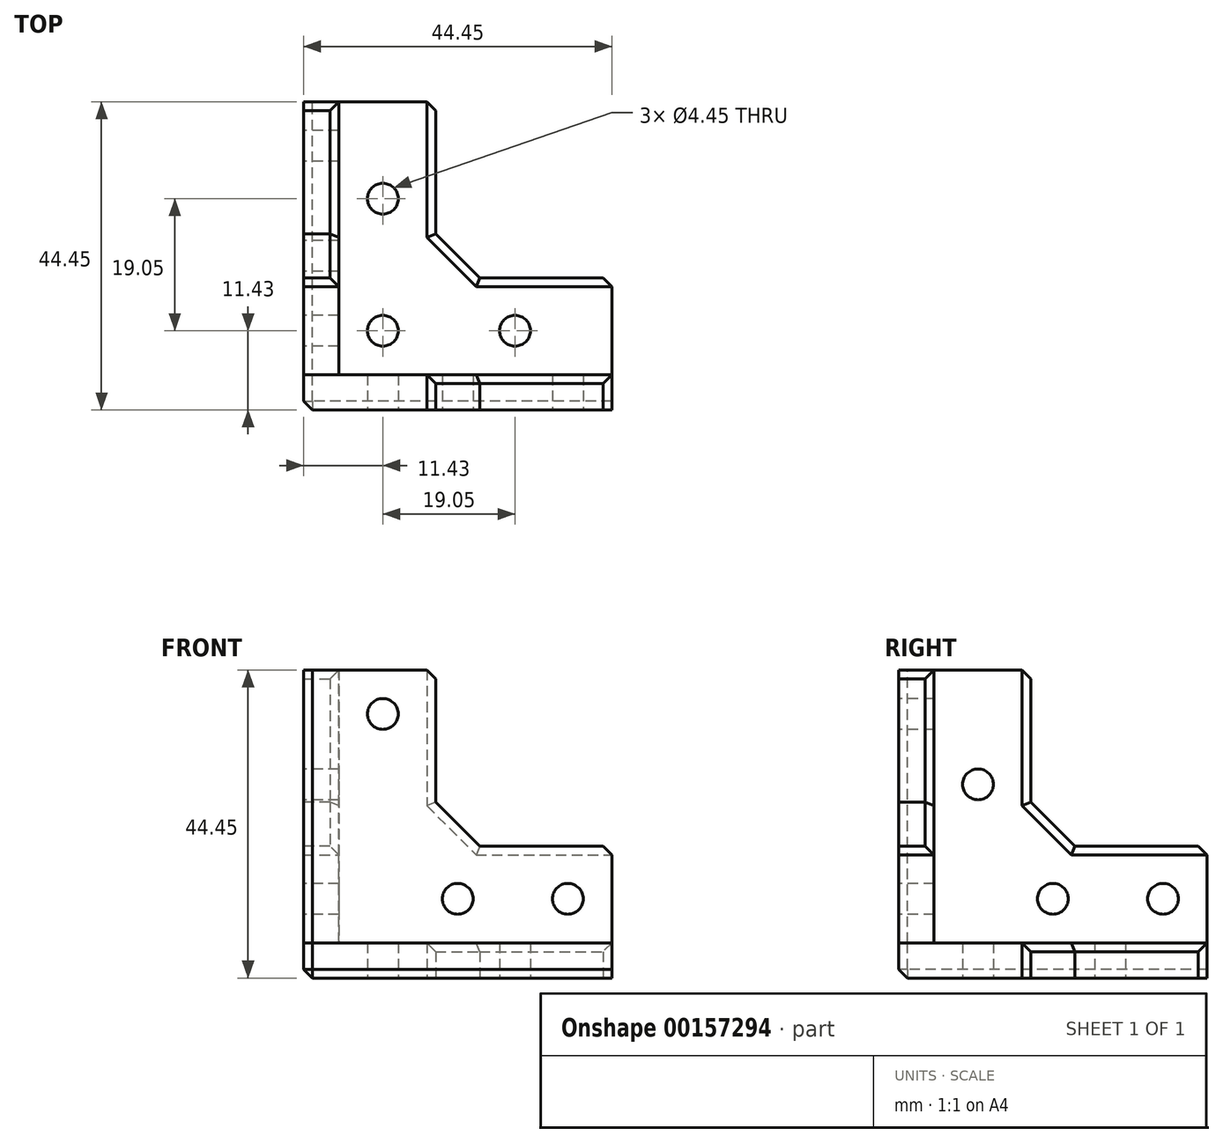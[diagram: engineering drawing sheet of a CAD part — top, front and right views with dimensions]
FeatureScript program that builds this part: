
annotation { "Feature Type Name" : "Feature", "Feature Type Description" : "" }
export const myFeature = defineFeature(function(context is Context, id is Id, definition is map)
    precondition{}
    {
        {
            var Q0;
            Q0=qCreatedBy(makeId("Top.planeOp"),FACE);
            var sketch = newSketch(context, id + "F0", { "sketchPlane" : qUnion([Q0])});
            skLineSegment(sketch, "E0", {"start": v(0, 0) * mm, "end": v(0, 44.45) * mm});
            skLineSegment(sketch, "E1", {"start": v(0, 44.45) * mm, "end": v(19.05, 44.45) * mm});
            skLineSegment(sketch, "E2", {"start": v(19.05, 44.45) * mm, "end": v(19.05, 25.4) * mm});
            skLineSegment(sketch, "E3", {"start": v(25.4, 19.05) * mm, "end": v(44.45, 19.05) * mm});
            skLineSegment(sketch, "E4", {"start": v(44.45, 19.05) * mm, "end": v(44.45, 0) * mm});
            skLineSegment(sketch, "E5", {"start": v(44.45, 0) * mm, "end": v(0, 0) * mm});
            skCircle(sketch, "E6", {"center": v(11.43, 30.48) * mm, "radius": 2.22 * mm});
            skCircle(sketch, "E7", {"center": v(11.43, 11.43) * mm, "radius": 2.22 * mm});
            skCircle(sketch, "E8", {"center": v(30.48, 11.43) * mm, "radius": 2.22 * mm});
            skLineSegment(sketch, "E9", {"start": v(19.05, 25.4) * mm, "end": v(25.4, 19.05) * mm});
            skSolve(sketch);
        }
        {
            var Q0;
            Q0 = qSketchRegion(id + "F0", true);
            extrude(context, id + "F1", {"entities" : qUnion([Q0]), "depth" : 5.08 * mm});
        }
        {
            var Q0;
            Q0=makeQuery(id+"F1.opExtrude","SWEPT_FACE",FACE,{"disambiguationData":[OSD([sQuery(id+"F0.wireOp",EDGE,"E5")])]});
            var sketch = newSketch(context, id + "F2", { "sketchPlane" : qUnion([Q0])});
            skLineSegment(sketch, "E10", {"start": v(0, 5.08) * mm, "end": v(0, 44.45) * mm});
            skLineSegment(sketch, "E11", {"start": v(0, 44.45) * mm, "end": v(19.05, 44.45) * mm});
            skLineSegment(sketch, "E12", {"start": v(19.05, 44.45) * mm, "end": v(19.05, 25.4) * mm});
            skLineSegment(sketch, "E13", {"start": v(25.4, 19.05) * mm, "end": v(44.45, 19.05) * mm});
            skLineSegment(sketch, "E14", {"start": v(44.45, 19.05) * mm, "end": v(44.45, 5.08) * mm});
            skLineSegment(sketch, "E15", {"start": v(0, 5.08) * mm, "end": v(44.45, 5.08) * mm});
            skCircle(sketch, "E16", {"center": v(11.43, 38.1) * mm, "radius": 2.22 * mm});
            skCircle(sketch, "E17", {"center": v(22.23, 11.43) * mm, "radius": 2.22 * mm});
            skCircle(sketch, "E18", {"center": v(38.1, 11.43) * mm, "radius": 2.22 * mm});
            skLineSegment(sketch, "E19", {"start": v(25.4, 19.05) * mm, "end": v(19.05, 25.4) * mm});
            skSolve(sketch);
        }
        {
            var Q0;
            Q0 = qSketchRegion(id + "F2", true);
            extrude(context, id + "F3", {"entities" : qUnion([Q0]), "oppositeDirection" : true, "depth" : 5.08 * mm});
        }
        {
            var Q0;
            Q0=makeQuery(id+"F1.opExtrude","SWEPT_FACE",FACE,{"disambiguationData":[OSD([sQuery(id+"F0.wireOp",EDGE,"E0")])]});
            var sketch = newSketch(context, id + "F4", { "sketchPlane" : qUnion([Q0])});
            skLineSegment(sketch, "E20", {"start": v(-44.45, 5.08) * mm, "end": v(-44.45, 19.05) * mm});
            skLineSegment(sketch, "E21", {"start": v(-44.45, 19.05) * mm, "end": v(-25.4, 19.05) * mm});
            skLineSegment(sketch, "E22", {"start": v(-19.05, 25.4) * mm, "end": v(-19.05, 44.45) * mm});
            skLineSegment(sketch, "E23", {"start": v(-19.05, 44.45) * mm, "end": v(-5.08, 44.45) * mm});
            skLineSegment(sketch, "E24", {"start": v(-5.08, 44.45) * mm, "end": v(-5.08, 5.08) * mm});
            skCircle(sketch, "E25", {"center": v(-11.43, 27.94) * mm, "radius": 2.22 * mm});
            skCircle(sketch, "E26", {"center": v(-38.1, 11.43) * mm, "radius": 2.22 * mm});
            skCircle(sketch, "E27", {"center": v(-22.23, 11.43) * mm, "radius": 2.22 * mm});
            skLineSegment(sketch, "E28", {"start": v(-25.4, 19.05) * mm, "end": v(-19.05, 25.4) * mm});
            skLineSegment(sketch, "E29", {"start": v(-44.45, 5.08) * mm, "end": v(-5.08, 5.08) * mm});
            skSolve(sketch);
        }
        {
            var Q0;
            Q0 = qSketchRegion(id + "F4", true);
            extrude(context, id + "F5", {"entities" : qUnion([Q0]), "oppositeDirection" : true, "depth" : 5.08 * mm});
        }
        {
            var Q0;
            Q0=makeQuery(id+"F1.opExtrude","CAP_EDGE",EDGE,{"disambiguationData":[OSD([sQuery(id+"F0.wireOp",EDGE,"E2")])],"isStart":false});
            var Q1;
            Q1=makeQuery(id+"F1.opExtrude","SWEPT_EDGE",EDGE,{"disambiguationData":[OSD([sQuery(id+"F0.wireOp",EDGE,"E1"),sQuery(id+"F0.wireOp",EDGE,"E2")])]});
            var Q2;
            Q2=makeQuery(id+"F5.opExtrude","SWEPT_EDGE",EDGE,{"disambiguationData":[OSD([sQuery(id+"F4.wireOp",EDGE,"E20"),sQuery(id+"F4.wireOp",EDGE,"E21")])]});
            var Q3;
            Q3=makeQuery(id+"F5.opExtrude","CAP_EDGE",EDGE,{"disambiguationData":[OSD([sQuery(id+"F4.wireOp",EDGE,"E21")])],"isStart":false});
            var Q4;
            Q4=makeQuery(id+"F5.opExtrude","CAP_EDGE",EDGE,{"disambiguationData":[OSD([sQuery(id+"F4.wireOp",EDGE,"E22")])],"isStart":false});
            var Q5;
            Q5=makeQuery(id+"F5.opExtrude","CAP_EDGE",EDGE,{"disambiguationData":[OSD([sQuery(id+"F4.wireOp",EDGE,"E28")])],"isStart":false});
            var Q6;
            Q6=makeQuery(id+"F5.opExtrude","SWEPT_EDGE",EDGE,{"disambiguationData":[OSD([sQuery(id+"F4.wireOp",EDGE,"E22"),sQuery(id+"F4.wireOp",EDGE,"E23")])]});
            var Q7;
            Q7=makeQuery(id+"F3.opExtrude","CAP_EDGE",EDGE,{"disambiguationData":[OSD([sQuery(id+"F2.wireOp",EDGE,"E12")])],"isStart":false});
            var Q8;
            Q8=makeQuery(id+"F3.opExtrude","CAP_EDGE",EDGE,{"disambiguationData":[OSD([sQuery(id+"F2.wireOp",EDGE,"E19")])],"isStart":false});
            var Q9;
            Q9=makeQuery(id+"F3.opExtrude","CAP_EDGE",EDGE,{"disambiguationData":[OSD([sQuery(id+"F2.wireOp",EDGE,"E13")])],"isStart":false});
            var Q10;
            Q10=makeQuery(id+"F1.opExtrude","CAP_EDGE",EDGE,{"disambiguationData":[OSD([sQuery(id+"F0.wireOp",EDGE,"E3")])],"isStart":false});
            var Q11;
            Q11=makeQuery(id+"F1.opExtrude","CAP_EDGE",EDGE,{"disambiguationData":[OSD([sQuery(id+"F0.wireOp",EDGE,"E9")])],"isStart":false});
            var Q12;
            Q12=makeQuery(id+"F1.opExtrude","SWEPT_EDGE",EDGE,{"disambiguationData":[OSD([sQuery(id+"F0.wireOp",EDGE,"E3"),sQuery(id+"F0.wireOp",EDGE,"E4")])]});
            var Q13;
            Q13=makeQuery(id+"F3.opExtrude","SWEPT_EDGE",EDGE,{"disambiguationData":[OSD([sQuery(id+"F2.wireOp",EDGE,"E13"),sQuery(id+"F2.wireOp",EDGE,"E14")])]});
            var Q14;
            Q14=makeQuery(id+"F3.opExtrude","SWEPT_EDGE",EDGE,{"disambiguationData":[OSD([sQuery(id+"F2.wireOp",EDGE,"E11"),sQuery(id+"F2.wireOp",EDGE,"E12")])]});
            var Q15;
            Q15=makeQuery(id+"F1.opExtrude","CAP_EDGE",EDGE,{"disambiguationData":[OSD([sQuery(id+"F0.wireOp",EDGE,"E5")])],"isStart":true});
            var Q16;
            Q16=makeQuery(id+"F1.opExtrude","SWEPT_EDGE",EDGE,{"disambiguationData":[OSD([sQuery(id+"F0.wireOp",EDGE,"E0"),sQuery(id+"F0.wireOp",EDGE,"E5")])]});
            var Q17;
            Q17=makeQuery(id+"F1.opExtrude","CAP_EDGE",EDGE,{"disambiguationData":[OSD([sQuery(id+"F0.wireOp",EDGE,"E0")])],"isStart":true});
            var Q18;
            Q18=makeQuery(id+"F3.opExtrude","CAP_EDGE",EDGE,{"disambiguationData":[OSD([sQuery(id+"F2.wireOp",EDGE,"E10")])],"isStart":true});
            chamfer(context, id + "F6", {"entities" : qUnion([Q0, Q1, Q2, Q3, Q4, Q5, Q6, Q7, Q8, Q9, Q10, Q11, Q12, Q13, Q14, Q15, Q16, Q17, Q18]), "width" : 1.27 * mm, "tangentPropagation" : true});
        }
    });
